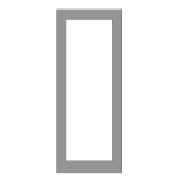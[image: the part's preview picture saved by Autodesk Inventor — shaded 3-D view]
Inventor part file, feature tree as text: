
AUTODESK INVENTOR PART (.ipt)
format: ipt  version: 2022.2 (Build 262287000, 287)  size: 145,920 bytes
history: native  units: in
note: dims shown in document units (in); Inventor stores cm internally (conversion verified against a paired STEP export)
features: other x4, sketch x4, hole x1, plane x1
ambient origin geometry x8: Origin, YZ Plane, XZ Plane, XY Plane, X Axis, Y Axis, Z Axis, Center Point
bodies: Solid1 (feature_tree), Body (feature_tree)
feature tree (10):
  other  "Driven Length"
  other  "Frame Generator"
  other  "Start Plane"
  other  "End Plane"
  sketch  "Sketch8"  dims[d3=0.125in]
  hole  "Hole1"  [1 undecoded]
  sketch  "Sketch"  dims[d6=-0.0in d7=20.0in d8=0.13in d9=0.0in d14=90.0deg d11=20.0in d16=0.25in d17=1.0in d18=1.0in d19=0.25in d20=1.0in d21=1.0in d22=0.1695in d23=0.75in d24=0.375in d25=0.06in d26=0.5635in d27=2.0in d28=0.8108in]
  sketch  "Sketch6"  dims[d0=1.0in d1=2.0in]
  plane  "Work Plane5"
  sketch  "Sketch7"  dims[d2=0.125in]
note: 1 required parameter value undecoded (feature->parameter linkage not recoverable at this tier; creation-order binding heuristic only, values carry confidence <= 0.55)
